# Revit family: IS_LDV_E2667_BIM_GB
name_source: partatom
category: Plumbing Fixtures
units: mm (PartAtom-declared; Revit-internal decimal feet)

## family parameters
Cut with Voids When Loaded = No
Host = Face
Maintain Annotation Orientation = No
OmniClass Number = 23.45.05.21.11.11
OmniClass Title = Water Operated Water Closets
Part Type = Normal
Room Calculation Point = No
Round Connector Dimension = Use Diameter
Shared = Yes

## types (1)
- E266701 - LDV SEAT&CVR SW SCL WHITE
    Accessories = https://www.idealstandard.co.uk
    AreaUnits = millimeters
    Assembly Code = C1030200
    AssetType = Fixed
    BIMObjectName = IS_LDV_ToiletSeat_E2667
    BREEAMApproved = No
    BarCode = 5017830562542
    Brand = Ideal Standard
    CWFU = 0
    ConnectionType = Plumbing
    Cost = 0 $
    Default Elevation = 400 mm  [stored 1.31234 ft]
    Description = La Dolce Vita®,  dedicated seat, sandwich, softlcose, easy-take off push button, adjustable hinge
    DurationUnit = year
    ECA = No
    EPD = https://www.idealstandard.co.uk
    ExpectedLife = 30
    Features = La Dolce Vita®,  dedicated seat, sandwich, softlcose, easy-take off push button, adjustable hinge
    Finish = white
    HWFU = 0
    Help = https://www.idealstandard.co.uk
    IfcExportAs = IfcSanitaryTerminalType
    IfcExportType = TOILETSEAT
    InstallationInstructions = https://www.idealstandard.co.uk
    LinearUnits = millimeters
    MAT = Ceramic_White_01
    Manufacturer = Ideal Standard
    ManufacturerURL = https://www.idealstandard.co.uk
    Model = E266701
    ModelNumber = E266701
    ModelReference = La Dolce Vita®,  dedicated seat, sandwich, softlcose, easy-take off push button, adjustable hinge
    NBSDescription = WC pans
    NBSReference = Pr_40_20_93_94
    Name = ToiletSeat_LDV_E2667_IdealStandard
    NettWeight = 2,2
    NominalDepth = 438 mm
    NominalHeight = 53 mm
    NominalLength = 438 mm
    NominalWidth = 373 mm
    PanColor = White
    PanMaterial = Duroplast
    PanMounting = BackToWall
    ProductInformation = https://www.idealstandard.co.uk
    Shape = Sculptured
    Size = 374 x 438 x 53 mm
    Space = Internal
    SpilloverLevel = 0 mm  [stored 0 ft]
    URL = https://www.idealstandard.co.uk
    Uniclass2015Code = Pr_40_20_93_94
    Uniclass2015Description = WC pans
    Uniclass2015Title = WC pans
    Uniclass2015Version = Products v1.33
    Version = 1
    VolumeUnits = Litres
    WFU = 0
    WRAS = No
    WarrantyDescription = Manufacturers Warranty
    WarrantyDurationParts = 99
    WarrantyDurationUnit = year
    WarrantyGuarantorParts = Ideal Standard
    WaterEfficientProduct = No

note: [stored X ft] marks values corroborated as IEEE doubles in the binary element streams (Revit-internal decimal feet)

## geometry (parser evidence)
native form markers: Sweep x2
no freeform markers — native parametric forms only
